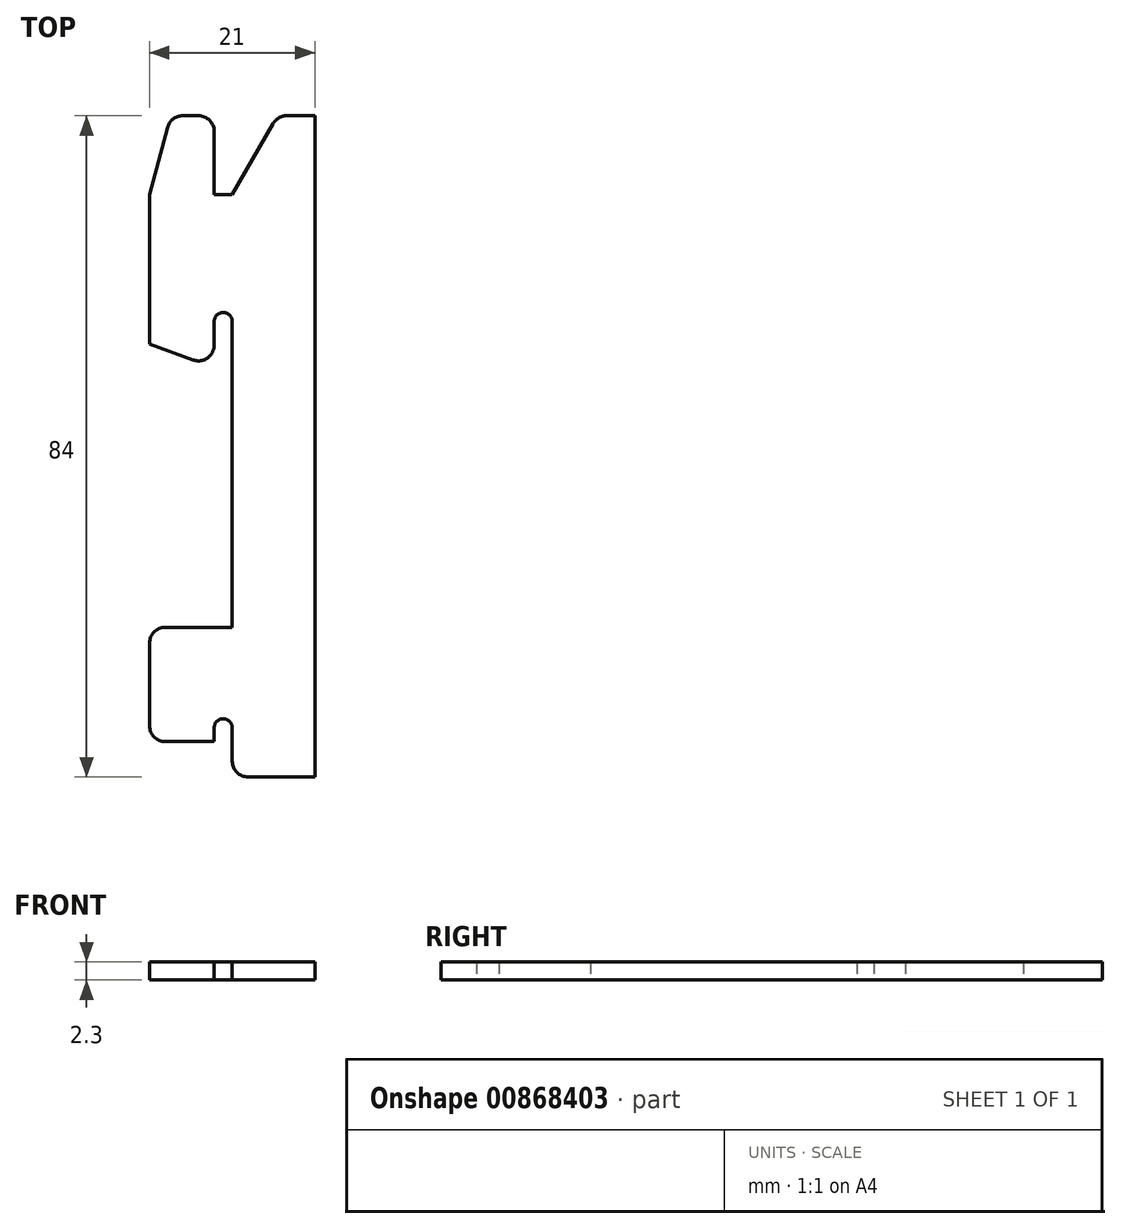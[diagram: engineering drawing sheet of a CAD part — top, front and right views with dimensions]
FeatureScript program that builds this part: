
annotation { "Feature Type Name" : "Feature", "Feature Type Description" : "" }
export const myFeature = defineFeature(function(context is Context, id is Id, definition is map)
    precondition{}
    {
        {
            var Q0;
            Q0=qCreatedBy(makeId("Top.planeOp"),FACE);
            var sketch = newSketch(context, id + "F0", { "sketchPlane" : qUnion([Q0])});
            skLineSegment(sketch, "E0", {"start": v(0, 0) * mm, "end": v(-8.5, 0) * mm});
            skLineSegment(sketch, "E1", {"start": v(-10.5, 2) * mm, "end": v(-10.5, 6.25) * mm});
            skLineSegment(sketch, "E2", {"start": v(-10.5, 6.25) * mm, "end": v(-12.8, 6.25) * mm, "construction": true});
            skLineSegment(sketch, "E3", {"start": v(-12.8, 6.25) * mm, "end": v(-12.8, 4.5) * mm});
            skLineSegment(sketch, "E4", {"start": v(-12.8, 4.5) * mm, "end": v(-19, 4.5) * mm});
            skLineSegment(sketch, "E5", {"start": v(-21, 6.5) * mm, "end": v(-21, 17) * mm});
            skLineSegment(sketch, "E6", {"start": v(-19, 19) * mm, "end": v(-10.5, 19) * mm});
            skLineSegment(sketch, "E7", {"start": v(-10.5, 19) * mm, "end": v(-10.5, 57.85) * mm});
            skLineSegment(sketch, "E8", {"start": v(-10.5, 57.85) * mm, "end": v(-12.8, 57.85) * mm, "construction": true});
            skLineSegment(sketch, "E9", {"start": v(-12.8, 57.85) * mm, "end": v(-12.8, 54.86) * mm});
            skLineSegment(sketch, "E10", {"start": v(-15.48, 52.98) * mm, "end": v(-21, 54.98) * mm});
            skLineSegment(sketch, "E11", {"start": v(-21, 54.98) * mm, "end": v(-21, 74) * mm});
            skLineSegment(sketch, "E12", {"start": v(-18.72, 82.52) * mm, "end": v(-21, 74) * mm});
            skLineSegment(sketch, "E13", {"start": v(-16.79, 84) * mm, "end": v(-14.8, 84) * mm});
            skLineSegment(sketch, "E14", {"start": v(-12.8, 82) * mm, "end": v(-12.8, 74) * mm});
            skLineSegment(sketch, "E15", {"start": v(-12.8, 74) * mm, "end": v(-10.5, 74) * mm});
            skLineSegment(sketch, "E16", {"start": v(-10.5, 74) * mm, "end": v(-5.3, 83) * mm});
            skLineSegment(sketch, "E17", {"start": v(-3.57, 84) * mm, "end": v(0, 84) * mm});
            skLineSegment(sketch, "E18", {"start": v(0, 84) * mm, "end": v(0, 0) * mm});
            skArc(sketch, "E19", {"start": v(-12.8, 6.25) * mm, "mid": v(-11.65, 7.4) * mm, "end": v(-10.5, 6.25) * mm});
            skLineSegment(sketch, "E20", {"start": v(-12.8, 4.5) * mm, "end": v(-12.8, 52) * mm, "construction": true});
            skLineSegment(sketch, "E21", {"start": v(-10.5, 6.25) * mm, "end": v(-10.5, 19) * mm, "construction": true});
            skArc(sketch, "E22", {"start": v(-12.8, 57.85) * mm, "mid": v(-11.65, 59) * mm, "end": v(-10.5, 57.85) * mm});
            skLineSegment(sketch, "E23", {"start": v(-21, 54.98) * mm, "end": v(-21, 19) * mm, "construction": true});
            skLineSegment(sketch, "E24", {"start": v(-12.8, 74) * mm, "end": v(-12.8, 57.85) * mm, "construction": true});
            skLineSegment(sketch, "E25", {"start": v(-10.5, 74) * mm, "end": v(-10.5, 57.85) * mm, "construction": true});
            skLineSegment(sketch, "E26", {"start": v(-12.8, 84) * mm, "end": v(-4.73, 84) * mm, "construction": true});
            skLineSegment(sketch, "E27", {"start": v(-12.8, 74) * mm, "end": v(-21, 74) * mm, "construction": true});
            skPoint(sketch, "E28.visualSharp", {"position": v(-21, 19) * mm});
            skArc(sketch, "E28.filletArc", {"start": v(-19, 19) * mm, "mid": v(-20.41, 18.41) * mm, "end": v(-21, 17) * mm});
            skPoint(sketch, "E29.visualSharp", {"position": v(-21, 4.5) * mm});
            skArc(sketch, "E29.filletArc", {"start": v(-21, 6.5) * mm, "mid": v(-20.41, 5.09) * mm, "end": v(-19, 4.5) * mm});
            skPoint(sketch, "E30.visualSharp", {"position": v(-12.8, 52) * mm});
            skArc(sketch, "E30.filletArc", {"start": v(-15.48, 52.98) * mm, "mid": v(-13.65, 53.22) * mm, "end": v(-12.8, 54.86) * mm});
            skPoint(sketch, "E31.visualSharp", {"position": v(-18.32, 84) * mm});
            skArc(sketch, "E31.filletArc", {"start": v(-16.79, 84) * mm, "mid": v(-18, 83.59) * mm, "end": v(-18.72, 82.52) * mm});
            skPoint(sketch, "E32.visualSharp", {"position": v(-12.8, 84) * mm});
            skArc(sketch, "E32.filletArc", {"start": v(-12.8, 82) * mm, "mid": v(-13.39, 83.41) * mm, "end": v(-14.8, 84) * mm});
            skPoint(sketch, "E33.visualSharp", {"position": v(-10.5, 0) * mm});
            skArc(sketch, "E33.filletArc", {"start": v(-10.5, 2) * mm, "mid": v(-9.91, 0.59) * mm, "end": v(-8.5, 0) * mm});
            skPoint(sketch, "E34.visualSharp", {"position": v(-4.73, 84) * mm});
            skArc(sketch, "E34.filletArc", {"start": v(-3.57, 84) * mm, "mid": v(-4.57, 83.73) * mm, "end": v(-5.3, 83) * mm});
            skSolve(sketch);
        }
        {
            var Q0;
            Q0=qSketchRegion(id+"F0",true);
            extrude(context, id + "F1", {"entities" : qUnion([Q0]), "depth" : 2.3 * mm, "offsetDistance" : 25 * mm});
        }
    });
